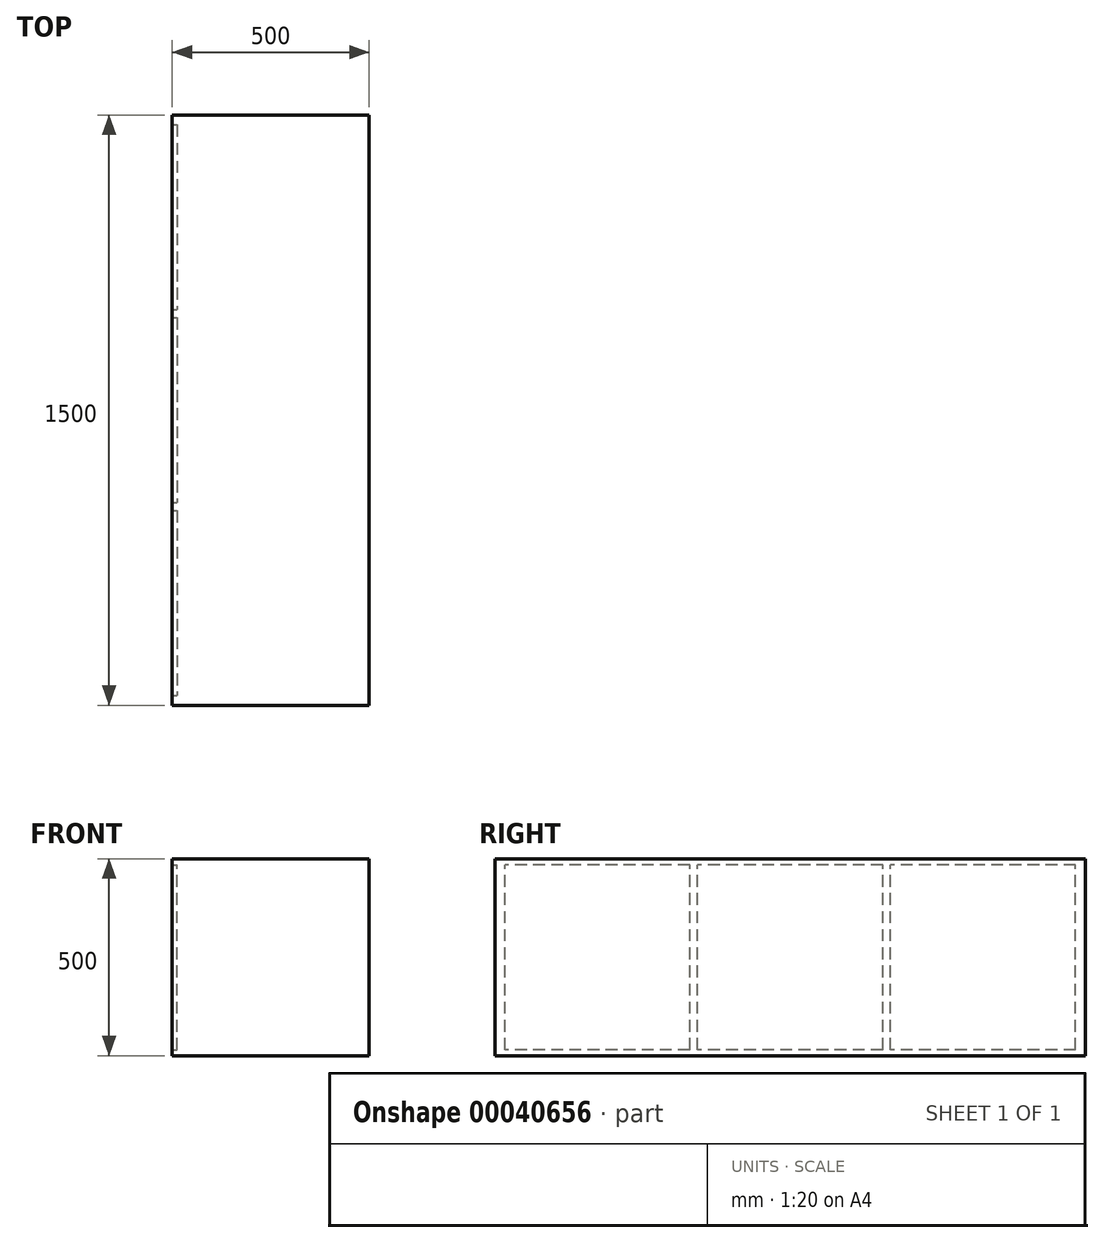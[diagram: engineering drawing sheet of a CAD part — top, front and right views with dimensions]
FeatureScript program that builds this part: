
annotation { "Feature Type Name" : "Feature", "Feature Type Description" : "" }
export const myFeature = defineFeature(function(context is Context, id is Id, definition is map)
    precondition{}
    {
        {
            var Q0;
            Q0=qCreatedBy(makeId("Right.planeOp"),FACE);
            var sketch = newSketch(context, id + "F0", { "sketchPlane" : qUnion([Q0])});
            skLineSegment(sketch, "E0.bottom", {"start": v(750, -250) * mm, "end": v(-750, -250) * mm});
            skLineSegment(sketch, "E0.top", {"start": v(750, 250) * mm, "end": v(-750, 250) * mm});
            skLineSegment(sketch, "E0.left", {"start": v(750, -250) * mm, "end": v(750, 250) * mm});
            skLineSegment(sketch, "E0.right", {"start": v(-750, -250) * mm, "end": v(-750, 250) * mm});
            skPoint(sketch, "E0.middle", {"position": v(0, 0) * mm});
            skLineSegment(sketch, "E1.bottom", {"start": v(-255, -235) * mm, "end": v(-725, -235) * mm});
            skLineSegment(sketch, "E1.top", {"start": v(-255, 235) * mm, "end": v(-725, 235) * mm});
            skLineSegment(sketch, "E1.left", {"start": v(-255, -235) * mm, "end": v(-255, 235) * mm});
            skLineSegment(sketch, "E1.right", {"start": v(-725, -235) * mm, "end": v(-725, 235) * mm});
            skPoint(sketch, "E1.middle", {"position": v(-490, 0) * mm});
            skLineSegment(sketch, "E2.bottom", {"start": v(235, -235) * mm, "end": v(-235, -235) * mm});
            skLineSegment(sketch, "E2.top", {"start": v(235, 235) * mm, "end": v(-235, 235) * mm});
            skLineSegment(sketch, "E2.left", {"start": v(235, -235) * mm, "end": v(235, 235) * mm});
            skLineSegment(sketch, "E2.right", {"start": v(-235, -235) * mm, "end": v(-235, 235) * mm});
            skLineSegment(sketch, "E3.bottom", {"start": v(725, -235) * mm, "end": v(255, -235) * mm});
            skLineSegment(sketch, "E3.top", {"start": v(725, 235) * mm, "end": v(255, 235) * mm});
            skLineSegment(sketch, "E3.left", {"start": v(725, -235) * mm, "end": v(725, 235) * mm});
            skLineSegment(sketch, "E3.right", {"start": v(255, -235) * mm, "end": v(255, 235) * mm});
            skPoint(sketch, "E3.middle", {"position": v(490, 0) * mm});
            skSolve(sketch);
        }
        {
            var Q0;
            Q0=makeQuery(id+"F0.imprint","IMPRINT",FACE,{"disambiguationData":[TD([[makeQuery(id+"F0.imprint","IMPRINT",EDGE,{"derivedFrom":sQuery(id+"F0.wireOp",EDGE,"E1.bottom")}),-1.0]])]});
            var Q1;
            Q1=makeQuery(id+"F0.imprint","IMPRINT",FACE,{"disambiguationData":[TD([[makeQuery(id+"F0.imprint","IMPRINT",EDGE,{"derivedFrom":sQuery(id+"F0.wireOp",EDGE,"E2.bottom")}),-1.0]])]});
            var Q2;
            Q2=makeQuery(id+"F0.imprint","IMPRINT",FACE,{"disambiguationData":[TD([[makeQuery(id+"F0.imprint","IMPRINT",EDGE,{"derivedFrom":sQuery(id+"F0.wireOp",EDGE,"E3.bottom")}),-1.0]])]});
            var Q3;
            Q3=makeQuery(id+"F0.imprint","IMPRINT",FACE,{"disambiguationData":[TD([[makeQuery(id+"F0.imprint","IMPRINT",EDGE,{"derivedFrom":sQuery(id+"F0.wireOp",EDGE,"E0.bottom")}),-1.0]])]});
            extrude(context, id + "F1", {"entities" : qUnion([Q0, Q1, Q2, Q3]), "depth" : 500 * mm});
        }
        {
            var Q0;
            Q0=makeQuery(id+"F0.imprint","IMPRINT",FACE,{"disambiguationData":[TD([[makeQuery(id+"F0.imprint","IMPRINT",EDGE,{"derivedFrom":sQuery(id+"F0.wireOp",EDGE,"E3.bottom")}),-1.0]])]});
            var Q1;
            Q1=makeQuery(id+"F0.imprint","IMPRINT",FACE,{"disambiguationData":[TD([[makeQuery(id+"F0.imprint","IMPRINT",EDGE,{"derivedFrom":sQuery(id+"F0.wireOp",EDGE,"E2.bottom")}),-1.0]])]});
            var Q2;
            Q2=makeQuery(id+"F0.imprint","IMPRINT",FACE,{"disambiguationData":[TD([[makeQuery(id+"F0.imprint","IMPRINT",EDGE,{"derivedFrom":sQuery(id+"F0.wireOp",EDGE,"E1.bottom")}),-1.0]])]});
            extrude(context, id + "F2", {"entities" : qUnion([Q0, Q1, Q2]), "operationType" : NewBodyOperationType.REMOVE, "oppositeDirection" : true, "depth" : 25 * mm, "symmetric" : true});
        }
    });
